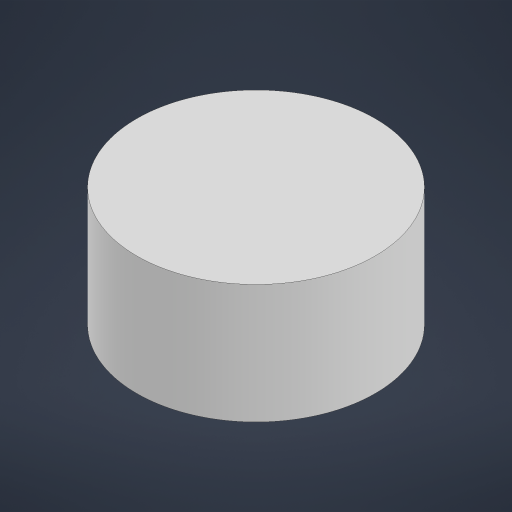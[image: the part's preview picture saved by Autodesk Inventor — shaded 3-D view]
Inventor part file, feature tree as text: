
AUTODESK INVENTOR PART (.ipt)
format: ipt  version: 2023 (Build 270158000, 158)  size: 142,336 bytes
history: native  units: in
note: dims shown in document units (in); Inventor stores cm internally (conversion verified against a paired STEP export)
features: extrude x1, sketch x1
ambient origin geometry x8: Origin, YZ Plane, XZ Plane, XY Plane, X Axis, Y Axis, Z Axis, Center Point
bodies: Solid1 (feature_tree)
feature tree (2):
  extrude  "Extrusion1"  Depth=1.0in TaperAngle=0.0deg
  sketch  "Sketch1"  dims[d0=2.0in d1=1.0in d2=0.0in]
